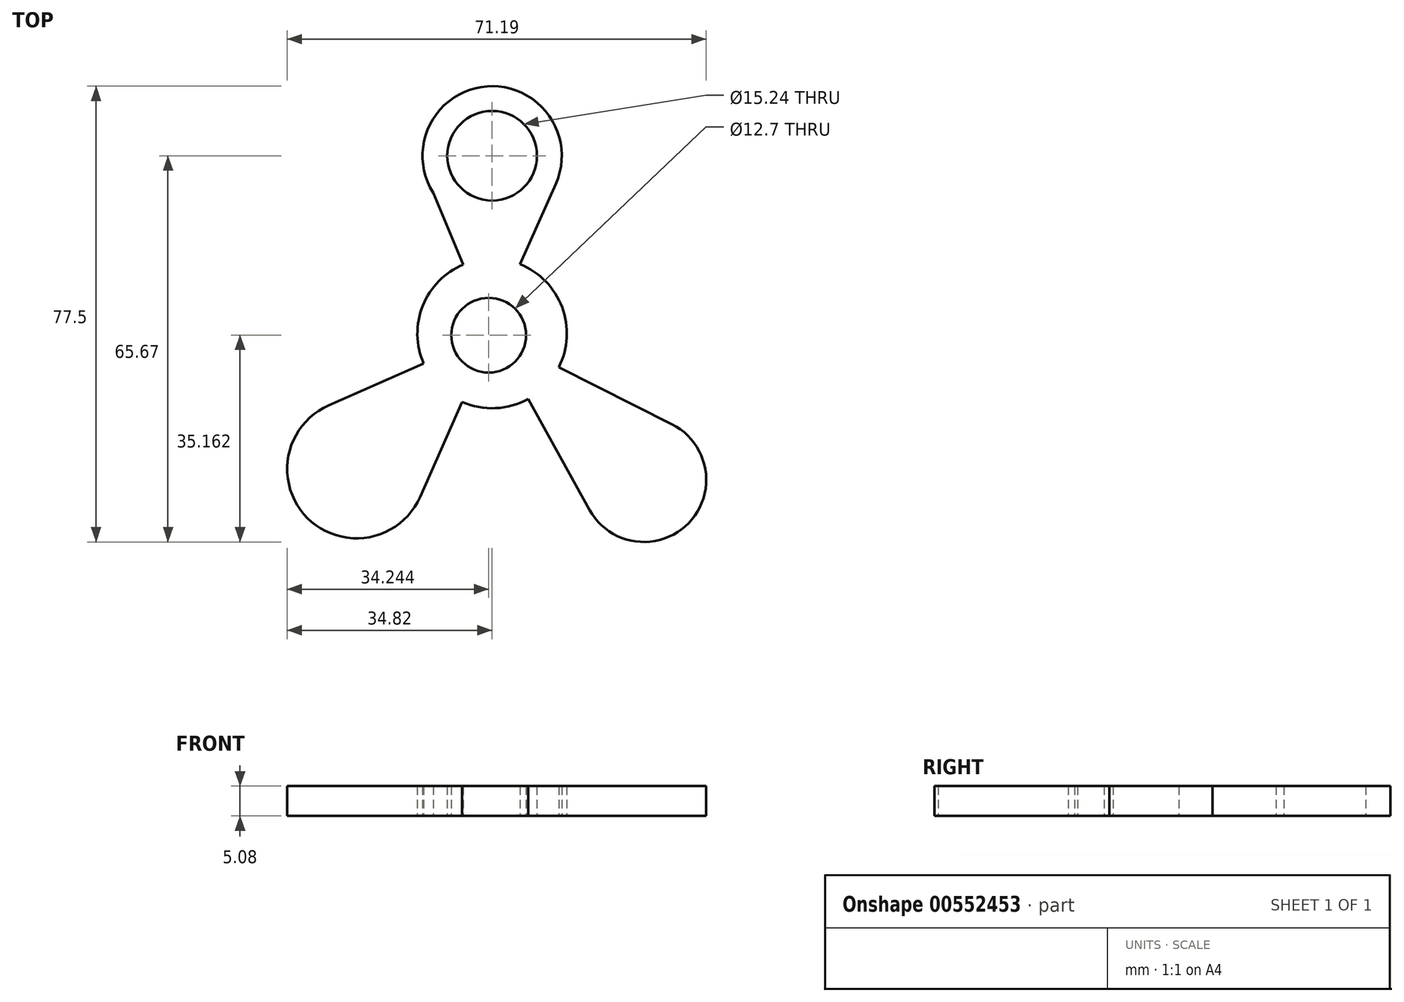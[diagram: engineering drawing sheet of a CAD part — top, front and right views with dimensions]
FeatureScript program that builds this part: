
annotation { "Feature Type Name" : "Feature", "Feature Type Description" : "" }
export const myFeature = defineFeature(function(context is Context, id is Id, definition is map)
    precondition{}
    {
        {
            var Q0;
            Q0=qCreatedBy(makeId("Top.planeOp"),FACE);
            var sketch = newSketch(context, id + "F0", { "sketchPlane" : qUnion([Q0])});
            skCircle(sketch, "E0", {"center": v(0, 0) * mm, "radius": 12.7 * mm});
            skSolve(sketch);
        }
        {
            var Q0;
            Q0=qSketchRegion(id+"F0",true);
            extrude(context, id + "F1", {"entities" : qUnion([Q0]), "depth" : 5.08 * mm, "offsetDistance" : 25.4 * mm});
        }
        {
            var Q0;
            Q0=qCreatedBy(makeId("Top.planeOp"),FACE);
            var sketch = newSketch(context, id + "F2", { "sketchPlane" : qUnion([Q0])});
            skCircle(sketch, "E1", {"center": v(0, 30.22) * mm, "radius": 11.83 * mm});
            skLineSegment(sketch, "E2", {"start": v(-10.02, 23.93) * mm, "end": v(0, 0) * mm});
            skLineSegment(sketch, "E3", {"start": v(-0.58, -0.29) * mm, "end": v(10.82, 25.43) * mm});
            skSolve(sketch);
        }
        {
            var Q0;
            Q0=qSketchRegion(id+"F2",true);
            extrude(context, id + "F3", {"entities" : qUnion([Q0]), "operationType" : NewBodyOperationType.ADD, "depth" : 5.08 * mm, "offsetDistance" : 25.4 * mm});
        }
        {
            var Q0;
            Q0=qCreatedBy(makeId("Top.planeOp"),FACE);
            var sketch = newSketch(context, id + "F4", { "sketchPlane" : qUnion([Q0])});
            skCircle(sketch, "E4", {"center": v(-23.02, -23.02) * mm, "radius": 11.8 * mm});
            skLineSegment(sketch, "E5", {"start": v(0, 0) * mm, "end": v(-27.78, -12.22) * mm});
            skLineSegment(sketch, "E6", {"start": v(0, 0) * mm, "end": v(-12.22, -27.78) * mm});
            skSolve(sketch);
        }
        {
            var Q0;
            Q0=qSketchRegion(id+"F4",true);
            extrude(context, id + "F5", {"entities" : qUnion([Q0]), "operationType" : NewBodyOperationType.ADD, "depth" : 5.08 * mm, "offsetDistance" : 25.4 * mm});
        }
        {
            var Q0;
            Q0=qCreatedBy(makeId("Top.planeOp"),FACE);
            var sketch = newSketch(context, id + "F6", { "sketchPlane" : qUnion([Q0])});
            skCircle(sketch, "E7", {"center": v(25.8, -24.87) * mm, "radius": 10.57 * mm});
            skLineSegment(sketch, "E8", {"start": v(0, 0) * mm, "end": v(16.54, -29.98) * mm});
            skLineSegment(sketch, "E9", {"start": v(0, 0) * mm, "end": v(30.57, -15.44) * mm});
            skSolve(sketch);
        }
        {
            var Q0;
            Q0=qSketchRegion(id+"F6",true);
            extrude(context, id + "F7", {"entities" : qUnion([Q0]), "operationType" : NewBodyOperationType.ADD, "depth" : 5.08 * mm, "offsetDistance" : 25.4 * mm});
        }
        {
            var Q0;
            Q0=sQuery(id+"F2.wireOp",VERTEX,"E1.center");
            var Q1;
            Q1=makeQuery(id+"F1.opExtrude","SWEPT_BODY",BODY,{"disambiguationData":[OSD([sQuery(id+"F0.wireOp",EDGE,"E0")])]});
            hole(context, id + "F8", {"style" : HoleStyle.SIMPLE, "endStyle" : HoleEndStyle.THROUGH, "oppositeDirection" : true, "holeDiameter" : 15.24 * mm, "isTappedThrough" : true, "tappedDepth" : 12.7 * mm, "tapClearance" : 3, "locations" : qUnion([Q0]), "scope" : qUnion([Q1])});
        }
        {
            var Q0;
            Q0=sQuery(id+"F2.wireOp",VERTEX,"E3.start");
            var Q1;
            Q1=makeQuery(id+"F1.opExtrude","SWEPT_BODY",BODY,{"disambiguationData":[OSD([sQuery(id+"F0.wireOp",EDGE,"E0")])]});
            hole(context, id + "F9", {"style" : HoleStyle.SIMPLE, "endStyle" : HoleEndStyle.THROUGH, "oppositeDirection" : true, "holeDiameter" : 12.7 * mm, "isTappedThrough" : true, "tappedDepth" : 12.7 * mm, "tapClearance" : 3, "locations" : qUnion([Q0]), "scope" : qUnion([Q1])});
        }
    });
